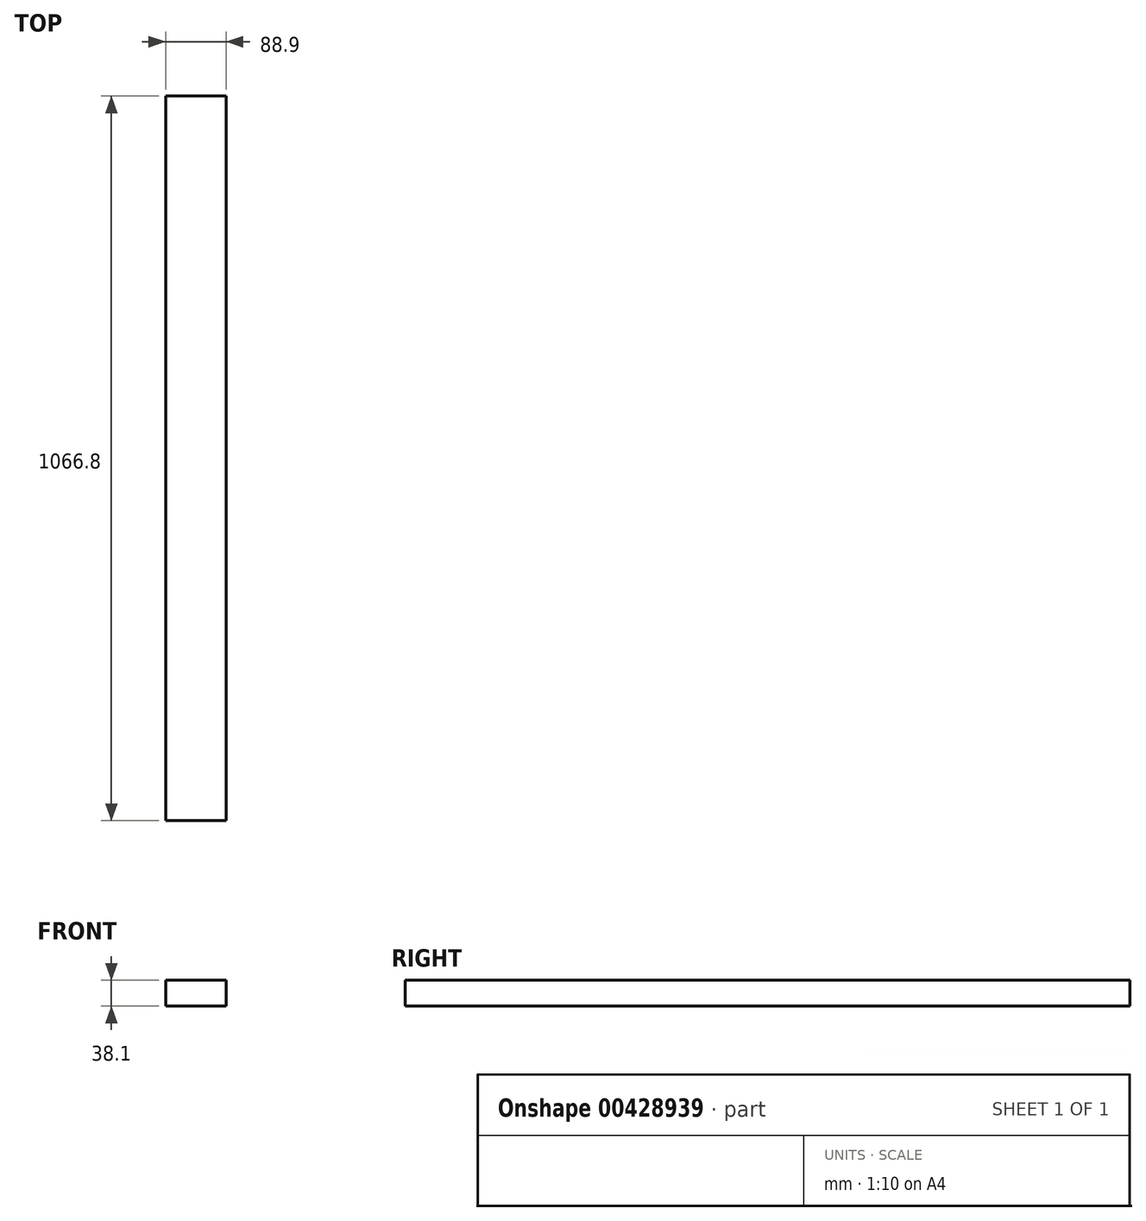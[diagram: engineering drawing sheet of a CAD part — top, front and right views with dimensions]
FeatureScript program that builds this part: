
annotation { "Feature Type Name" : "Feature", "Feature Type Description" : "" }
export const myFeature = defineFeature(function(context is Context, id is Id, definition is map)
    precondition{}
    {
        {
            var Q0;
            Q0=qCreatedBy(makeId("Top.planeOp"),FACE);
            var sketch = newSketch(context, id + "F0", { "sketchPlane" : qUnion([Q0])});
            skLineSegment(sketch, "E0.bottom", {"start": v(-107.24, 1012.6) * mm, "end": v(-18.34, 1012.6) * mm});
            skLineSegment(sketch, "E0.top", {"start": v(-107.24, -54.2) * mm, "end": v(-18.34, -54.2) * mm});
            skLineSegment(sketch, "E0.left", {"start": v(-107.24, 1012.6) * mm, "end": v(-107.24, -54.2) * mm});
            skLineSegment(sketch, "E0.right", {"start": v(-18.34, 1012.6) * mm, "end": v(-18.34, -54.2) * mm});
            skSolve(sketch);
        }
        {
            var Q0;
            Q0=makeQuery(id+"F0.imprint","IMPRINT",FACE,{"disambiguationData":[TD([[makeQuery(id+"F0.imprint","IMPRINT",EDGE,{"derivedFrom":sQuery(id+"F0.wireOp",EDGE,"E0.bottom")}),-1.0]])]});
            extrude(context, id + "F1", {"entities" : qUnion([Q0]), "depth" : 38.1 * mm});
        }
    });
